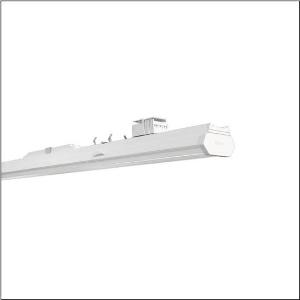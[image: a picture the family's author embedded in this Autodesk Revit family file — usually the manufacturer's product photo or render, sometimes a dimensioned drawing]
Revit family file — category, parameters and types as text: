
# Revit family: licross_r__21_protected_ho_52td12dn4dxm_7c2c
name_source: partatom
category: Lighting Fixtures
units: mm (PartAtom-declared; Revit-internal decimal feet)

## family parameters
Cut with Voids When Loaded = No
Host = Face
Light Source = No
Part Type = Normal
Room Calculation Point = No
Round Connector Dimension = Use Diameter
Shared = No

## types (1)
- --- (1 x LED, 13000 lm, 74.3 W, 4000K)
    Apparent Load = 74 VA
    CIE Flux Codes = 70 91 97 98 100
    Color Rendering = 80
    Color Temperature = 4000K
    Default Elevation = 1800 mm
    Description = Licross® 21 Protected HO, luminaire insert, of sheet steel, galvanised, coil coated, white, length: 1.500mm, width: 90mm, height: 103mm, LED rated luminous flux: 13.000lm, light colour: 840, control gear: DALI 2, with plug, 5-pole, with phase selection, mains connection: 220..240V, AC, 50/60Hz, rated input power: 74W, halogen-free wiring, primary light control with lens, of plastic, primary optical cover: cover, of PMMA, light emission: direct distribution, primary light characteristic: symmetric, protection rating (complete): IP54, insulation class (complete): insulation class I (protective earthing), certification: CE, ENEC, VDE, UKCA, protection symbol: D if used in an environment with non-conductive dust loads with corresponding accessories, impact resistance: IK06, permissible ambient temperature for indoor applications: -25..+40°C, corresponds to IFS (International Featured Standards) requirements for safety and quality in the food industry, reducing of maximum allowable ambient temperature of 5°C with ceiling mounting, LABS conformity tested according to VDMA 24364:2018-05, packaging unit: 1 piece
    Height = 92 mm
    Lamp = 1 x LED
    Lamp Light Flux = 13000 lm
    Lamp Power = 74.3 W
    Lamp count = 1
    Length = 1500 mm
    Luminous efficacy = 175 lm/W
    Manufacturer = Siteco
    ModVariant = No
    Model = 52TD12DN4DXM
    Mounting Place = Ceiling
    Mounting Type = Pendant
    Number of Poles = 1
    OnlyDefault = Yes
    Power Factor = 1
    Product Name = Licross® 21 Protected HO
    Product group = luminaire insert
    ProductGroupID = 901
    Protection Class = Protection class I
    Protection Degree = IP 54
    RLX_Detail_Level = 1
    RLX_Emergency_Light_Flux = 0 lm
    RLX_Emergency_Type = 0
    RLX_Emergency_Type_DB = No
    RlxData = <blob elided: 24469 chars, md5=e9e0136e>
    Socket = socket
    Standby Power = 0 W
    System Light Flux = 13000 lm
    System Power = 74 W
    Type Comments = factory setting: luminous flux: 100 % | dim-lin: 254 | 424 mA
    Type Image = l_1256148.jpg
    URL = http://relux.com
    VarID = @adj_060539
    Voltage = 0 V
    Weight = 0.00 kg
    Width = 88 mm

## geometry (parser evidence)
native form markers: Blend x4, Sweep x9
no freeform markers — native parametric forms only
